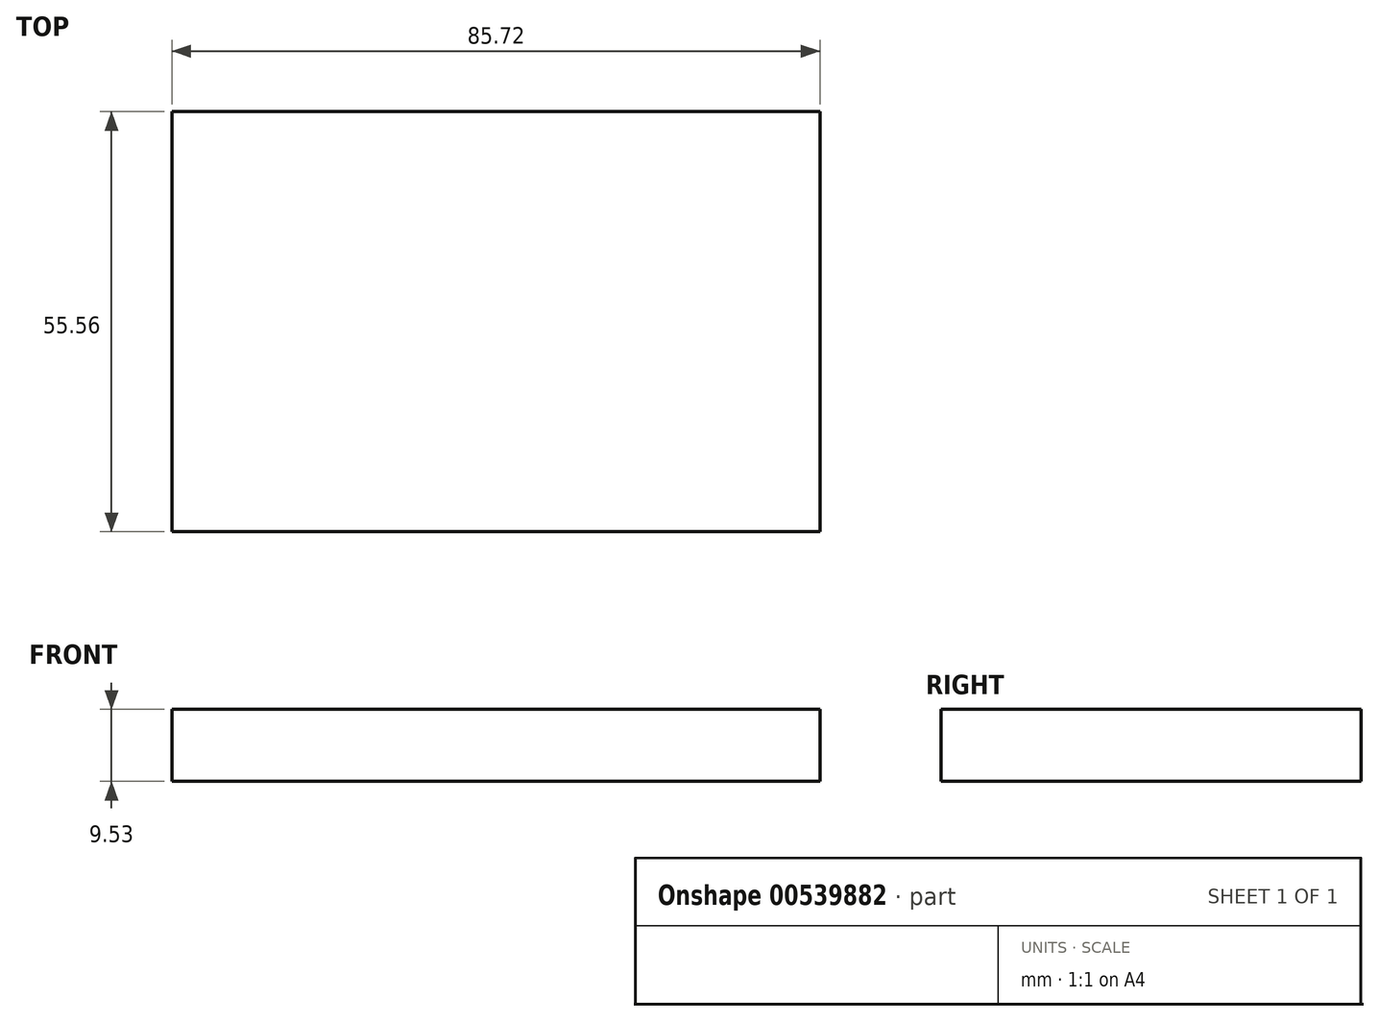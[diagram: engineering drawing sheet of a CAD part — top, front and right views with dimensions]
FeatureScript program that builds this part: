
annotation { "Feature Type Name" : "Feature", "Feature Type Description" : "" }
export const myFeature = defineFeature(function(context is Context, id is Id, definition is map)
    precondition{}
    {
        {
            var Q0;
            Q0=qCreatedBy(makeId("Top.planeOp"),FACE);
            var sketch = newSketch(context, id + "F0", { "sketchPlane" : qUnion([Q0])});
            skLineSegment(sketch, "E0.bottom", {"start": v(42.86, 27.78) * mm, "end": v(-42.86, 27.78) * mm});
            skLineSegment(sketch, "E0.top", {"start": v(42.86, -27.78) * mm, "end": v(-42.86, -27.78) * mm});
            skLineSegment(sketch, "E0.left", {"start": v(42.86, 27.78) * mm, "end": v(42.86, -27.78) * mm});
            skLineSegment(sketch, "E0.right", {"start": v(-42.86, 27.78) * mm, "end": v(-42.86, -27.78) * mm});
            skPoint(sketch, "E0.middle", {"position": v(0, 0) * mm});
            skSolve(sketch);
        }
        {
            var Q0;
            Q0=makeQuery(id+"F0.imprint","IMPRINT",FACE,{"disambiguationData":[TD([[makeQuery(id+"F0.imprint","IMPRINT",EDGE,{"derivedFrom":sQuery(id+"F0.wireOp",EDGE,"E0.bottom")}),1.0]])]});
            extrude(context, id + "F1", {"entities" : qUnion([Q0]), "depth" : 9.52 * mm, "offsetDistance" : 25.4 * mm});
        }
    });
